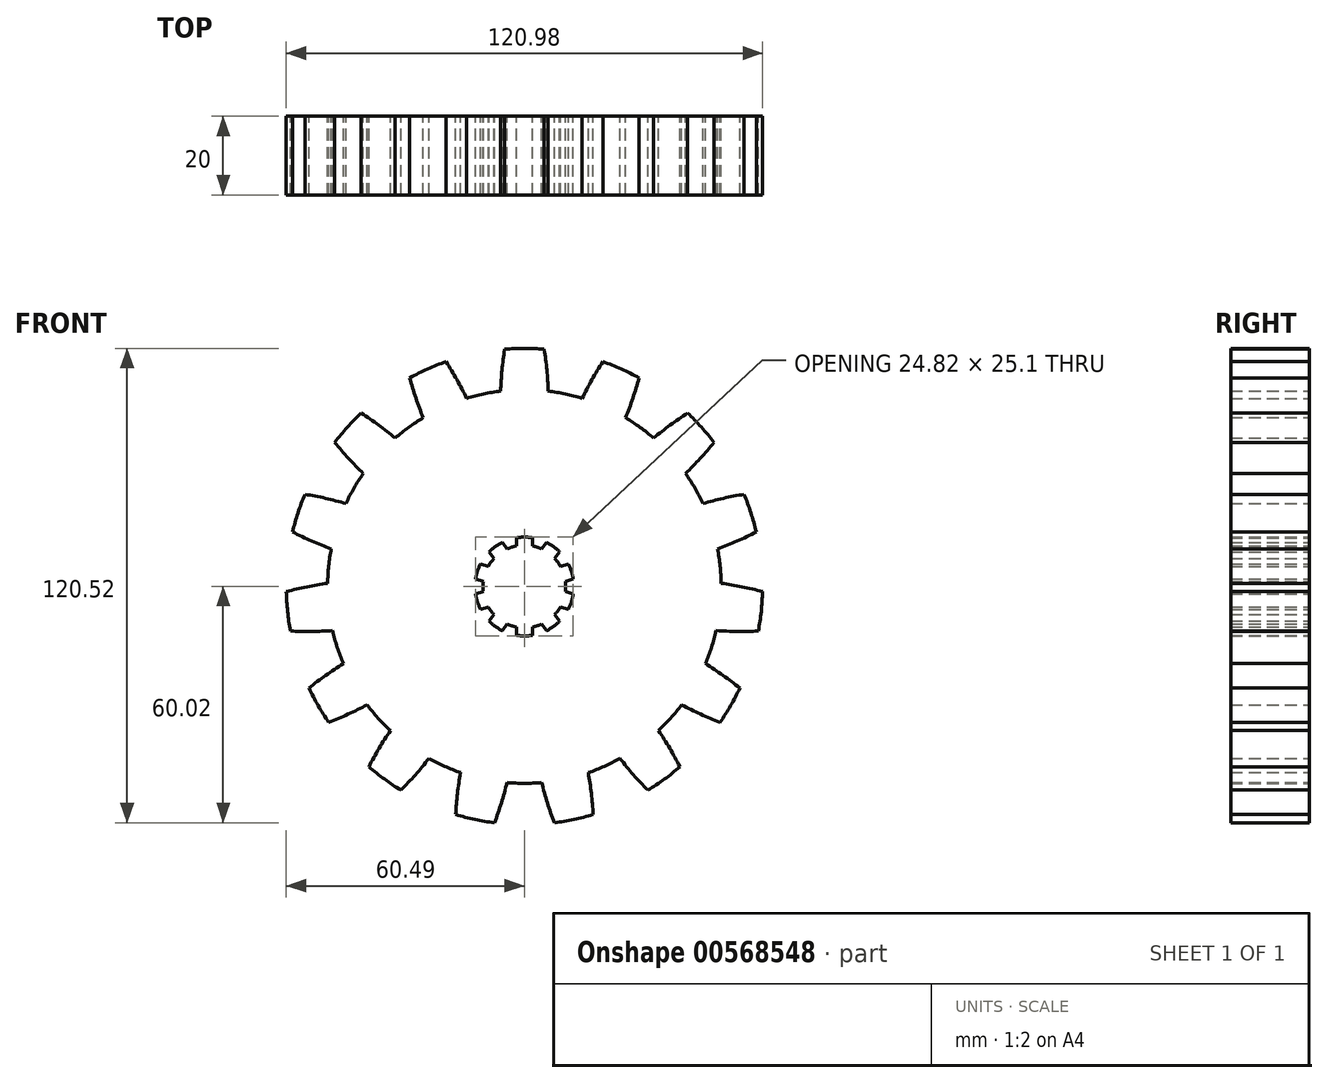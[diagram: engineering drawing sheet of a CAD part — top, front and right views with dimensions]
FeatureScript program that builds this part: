
annotation { "Feature Type Name" : "Feature", "Feature Type Description" : "" }
export const myFeature = defineFeature(function(context is Context, id is Id, definition is map)
    precondition{}
    {
        {
            var Q0;
            Q0=qCreatedBy(makeId("Front.planeOp"),FACE);
            var sketch = newSketch(context, id + "F0", { "sketchPlane" : qUnion([Q0])});
            skArc(sketch, "E0", {"start": v(-49.07, 9.59) * mm, "mid": v(-49.73, 5.23) * mm, "end": v(-50, 0.82) * mm});
            skLineSegment(sketch, "E1", {"start": v(0, 54.02) * mm, "end": v(0, -56.45) * mm, "construction": true});
            skLineSegment(sketch, "E2", {"start": v(-55.52, 46.5) * mm, "end": v(83.9, 46.5) * mm, "construction": true});
            skArc(sketch, "E3", {"start": v(5.04, 60.29) * mm, "mid": v(0, 60.5) * mm, "end": v(-5.04, 60.29) * mm});
            skArc(sketch, "E4.trimOffspring", {"start": v(-5.04, 60.29) * mm, "mid": v(-5.7, 54.98) * mm, "end": v(-6.05, 49.63) * mm});
            skArc(sketch, "E5.MirrorCS", {"start": v(5.04, 60.29) * mm, "mid": v(5.7, 54.98) * mm, "end": v(6.05, 49.63) * mm});
            skArc(sketch, "E6.1.0", {"start": v(-19.92, 57.13) * mm, "mid": v(-17.15, 52.54) * mm, "end": v(-14.66, 47.8) * mm});
            skArc(sketch, "E6.1.1", {"start": v(-29.12, 53.03) * mm, "mid": v(-27.57, 47.9) * mm, "end": v(-25.71, 42.88) * mm});
            skArc(sketch, "E6.1.2", {"start": v(-19.92, 57.13) * mm, "mid": v(-24.6, 55.27) * mm, "end": v(-29.12, 53.03) * mm});
            skArc(sketch, "E6.2.0", {"start": v(-41.43, 44.09) * mm, "mid": v(-37.04, 41.02) * mm, "end": v(-32.84, 37.7) * mm});
            skArc(sketch, "E6.2.1", {"start": v(-48.17, 36.6) * mm, "mid": v(-44.67, 32.55) * mm, "end": v(-40.93, 28.72) * mm});
            skArc(sketch, "E6.2.2", {"start": v(-41.43, 44.09) * mm, "mid": v(-44.96, 40.48) * mm, "end": v(-48.17, 36.6) * mm});
            skArc(sketch, "E6.3.0", {"start": v(-55.78, 23.42) * mm, "mid": v(-50.52, 22.4) * mm, "end": v(-45.34, 21.09) * mm});
            skArc(sketch, "E6.3.1", {"start": v(-58.9, 13.84) * mm, "mid": v(-54.05, 11.57) * mm, "end": v(-49.07, 9.59) * mm});
            skArc(sketch, "E6.3.2", {"start": v(-55.78, 23.42) * mm, "mid": v(-57.54, 18.7) * mm, "end": v(-58.9, 13.84) * mm});
            skArc(sketch, "E6.4.0", {"start": v(-60.49, -1.3) * mm, "mid": v(-55.27, -0.08) * mm, "end": v(-50, 0.82) * mm});
            skArc(sketch, "E6.4.1", {"start": v(-59.43, -11.31) * mm, "mid": v(-54.08, -11.42) * mm, "end": v(-48.73, -11.2) * mm});
            skArc(sketch, "E6.4.2", {"start": v(-60.49, -1.3) * mm, "mid": v(-60.17, -6.32) * mm, "end": v(-59.43, -11.31) * mm});
            skArc(sketch, "E6.5.0", {"start": v(-54.73, -25.78) * mm, "mid": v(-50.46, -22.55) * mm, "end": v(-46, -19.58) * mm});
            skArc(sketch, "E6.5.1", {"start": v(-49.7, -34.5) * mm, "mid": v(-44.76, -32.42) * mm, "end": v(-39.96, -30.05) * mm});
            skArc(sketch, "E6.5.2", {"start": v(-54.73, -25.78) * mm, "mid": v(-52.4, -30.25) * mm, "end": v(-49.7, -34.5) * mm});
            skArc(sketch, "E6.6.0", {"start": v(-39.51, -45.81) * mm, "mid": v(-36.93, -41.13) * mm, "end": v(-34.06, -36.6) * mm});
            skArc(sketch, "E6.6.1", {"start": v(-31.36, -51.74) * mm, "mid": v(-27.7, -47.83) * mm, "end": v(-24.28, -43.7) * mm});
            skArc(sketch, "E6.6.2", {"start": v(-39.51, -45.81) * mm, "mid": v(-35.56, -48.95) * mm, "end": v(-31.36, -51.74) * mm});
            skArc(sketch, "E6.7.0", {"start": v(-17.46, -57.93) * mm, "mid": v(-17, -52.6) * mm, "end": v(-16.23, -47.3) * mm});
            skArc(sketch, "E6.7.1", {"start": v(-7.6, -60.02) * mm, "mid": v(-5.85, -54.96) * mm, "end": v(-4.4, -49.8) * mm});
            skArc(sketch, "E6.7.2", {"start": v(-17.46, -57.93) * mm, "mid": v(-12.58, -59.18) * mm, "end": v(-7.6, -60.02) * mm});
            skArc(sketch, "E6.8.0", {"start": v(7.6, -60.02) * mm, "mid": v(5.85, -54.96) * mm, "end": v(4.4, -49.8) * mm});
            skArc(sketch, "E6.8.1", {"start": v(17.46, -57.93) * mm, "mid": v(17, -52.6) * mm, "end": v(16.23, -47.3) * mm});
            skArc(sketch, "E6.8.2", {"start": v(7.6, -60.02) * mm, "mid": v(12.58, -59.18) * mm, "end": v(17.46, -57.93) * mm});
            skArc(sketch, "E6.9.0", {"start": v(31.36, -51.74) * mm, "mid": v(27.7, -47.83) * mm, "end": v(24.28, -43.7) * mm});
            skArc(sketch, "E6.9.1", {"start": v(39.51, -45.81) * mm, "mid": v(36.93, -41.13) * mm, "end": v(34.06, -36.6) * mm});
            skArc(sketch, "E6.9.2", {"start": v(31.36, -51.74) * mm, "mid": v(35.56, -48.95) * mm, "end": v(39.51, -45.81) * mm});
            skArc(sketch, "E6.10.0", {"start": v(49.7, -34.5) * mm, "mid": v(44.76, -32.42) * mm, "end": v(39.96, -30.05) * mm});
            skArc(sketch, "E6.10.1", {"start": v(54.73, -25.78) * mm, "mid": v(50.46, -22.55) * mm, "end": v(46, -19.58) * mm});
            skArc(sketch, "E6.10.2", {"start": v(49.7, -34.5) * mm, "mid": v(52.4, -30.25) * mm, "end": v(54.73, -25.78) * mm});
            skArc(sketch, "E6.11.0", {"start": v(59.43, -11.31) * mm, "mid": v(54.08, -11.42) * mm, "end": v(48.73, -11.2) * mm});
            skArc(sketch, "E6.11.1", {"start": v(60.49, -1.3) * mm, "mid": v(55.27, -0.08) * mm, "end": v(50, 0.82) * mm});
            skArc(sketch, "E6.11.2", {"start": v(59.43, -11.31) * mm, "mid": v(60.17, -6.32) * mm, "end": v(60.49, -1.3) * mm});
            skArc(sketch, "E6.12.0", {"start": v(58.9, 13.84) * mm, "mid": v(54.05, 11.57) * mm, "end": v(49.07, 9.59) * mm});
            skArc(sketch, "E6.12.1", {"start": v(55.78, 23.42) * mm, "mid": v(50.52, 22.4) * mm, "end": v(45.34, 21.09) * mm});
            skArc(sketch, "E6.12.2", {"start": v(58.9, 13.84) * mm, "mid": v(57.54, 18.7) * mm, "end": v(55.78, 23.42) * mm});
            skArc(sketch, "E6.13.0", {"start": v(48.17, 36.6) * mm, "mid": v(44.67, 32.55) * mm, "end": v(40.93, 28.72) * mm});
            skArc(sketch, "E6.13.1", {"start": v(41.43, 44.09) * mm, "mid": v(37.04, 41.02) * mm, "end": v(32.84, 37.7) * mm});
            skArc(sketch, "E6.13.2", {"start": v(48.17, 36.6) * mm, "mid": v(44.96, 40.48) * mm, "end": v(41.43, 44.09) * mm});
            skArc(sketch, "E6.14.0", {"start": v(29.12, 53.03) * mm, "mid": v(27.57, 47.9) * mm, "end": v(25.71, 42.88) * mm});
            skArc(sketch, "E6.14.1", {"start": v(19.92, 57.13) * mm, "mid": v(17.15, 52.54) * mm, "end": v(14.66, 47.8) * mm});
            skArc(sketch, "E6.14.2", {"start": v(29.12, 53.03) * mm, "mid": v(24.6, 55.27) * mm, "end": v(19.92, 57.13) * mm});
            skArc(sketch, "E7.trimOffspring", {"start": v(-40.93, 28.72) * mm, "mid": v(-43.3, 25) * mm, "end": v(-45.34, 21.09) * mm});
            skArc(sketch, "E8.trimOffspring", {"start": v(-25.71, 42.88) * mm, "mid": v(-29.39, 40.45) * mm, "end": v(-32.84, 37.7) * mm});
            skArc(sketch, "E9.trimOffspring", {"start": v(-6.05, 49.63) * mm, "mid": v(-10.4, 48.9) * mm, "end": v(-14.66, 47.8) * mm});
            skArc(sketch, "E10.trimOffspring", {"start": v(14.66, 47.8) * mm, "mid": v(10.4, 48.9) * mm, "end": v(6.05, 49.63) * mm});
            skArc(sketch, "E11.trimOffspring", {"start": v(32.84, 37.7) * mm, "mid": v(29.39, 40.45) * mm, "end": v(25.71, 42.88) * mm});
            skArc(sketch, "E12.trimOffspring", {"start": v(45.34, 21.09) * mm, "mid": v(43.3, 25) * mm, "end": v(40.93, 28.72) * mm});
            skArc(sketch, "E13.trimOffspring", {"start": v(50, 0.82) * mm, "mid": v(49.73, 5.23) * mm, "end": v(49.07, 9.59) * mm});
            skArc(sketch, "E14.trimOffspring", {"start": v(46, -19.58) * mm, "mid": v(47.55, -15.45) * mm, "end": v(48.73, -11.2) * mm});
            skArc(sketch, "E15.trimOffspring", {"start": v(34.06, -36.6) * mm, "mid": v(37.16, -33.46) * mm, "end": v(39.96, -30.05) * mm});
            skArc(sketch, "E16.trimOffspring", {"start": v(16.23, -47.3) * mm, "mid": v(20.34, -45.68) * mm, "end": v(24.28, -43.7) * mm});
            skArc(sketch, "E17.trimOffspring", {"start": v(-4.4, -49.8) * mm, "mid": v(0, -50) * mm, "end": v(4.4, -49.8) * mm});
            skArc(sketch, "E18.trimOffspring", {"start": v(-24.28, -43.7) * mm, "mid": v(-20.34, -45.68) * mm, "end": v(-16.23, -47.3) * mm});
            skArc(sketch, "E19.trimOffspring", {"start": v(-39.96, -30.05) * mm, "mid": v(-37.16, -33.46) * mm, "end": v(-34.06, -36.6) * mm});
            skArc(sketch, "E20.trimOffspring", {"start": v(-48.73, -11.2) * mm, "mid": v(-47.55, -15.45) * mm, "end": v(-46, -19.58) * mm});
            skSolve(sketch);
        }
        {
            var Q0;
            Q0 = qSketchRegion(id + "F0", true);
            extrude(context, id + "F1", {"entities" : qUnion([Q0]), "depth" : 20 * mm, "offsetDistance" : 25 * mm});
        }
        {
            var Q0;
            Q0=qCreatedBy(makeId("Front.planeOp"),FACE);
            var sketch = newSketch(context, id + "F2", { "sketchPlane" : qUnion([Q0])});
            skCircle(sketch, "E21", {"center": v(0, 0) * mm, "radius": 10.5 * mm});
            skArc(sketch, "E22", {"start": v(2.05, 12.38) * mm, "mid": v(0, 12.55) * mm, "end": v(-2.05, 12.38) * mm});
            skLineSegment(sketch, "E23", {"start": v(2.05, 10.3) * mm, "end": v(2.05, 12.38) * mm});
            skLineSegment(sketch, "E24", {"start": v(-2.05, 10.3) * mm, "end": v(-2.05, 12.38) * mm});
            skArc(sketch, "E25.1.0", {"start": v(-5.62, 11.22) * mm, "mid": v(-7.38, 10.15) * mm, "end": v(-8.94, 8.81) * mm});
            skLineSegment(sketch, "E25.1.1", {"start": v(-4.4, 9.54) * mm, "end": v(-5.62, 11.22) * mm});
            skLineSegment(sketch, "E25.1.2", {"start": v(-7.71, 7.13) * mm, "end": v(-8.94, 8.81) * mm});
            skArc(sketch, "E25.2.0", {"start": v(-11.14, 5.78) * mm, "mid": v(-11.94, 3.88) * mm, "end": v(-12.4, 1.88) * mm});
            skLineSegment(sketch, "E25.2.1", {"start": v(-9.16, 5.13) * mm, "end": v(-11.14, 5.78) * mm});
            skLineSegment(sketch, "E25.2.2", {"start": v(-10.43, 1.23) * mm, "end": v(-12.4, 1.88) * mm});
            skArc(sketch, "E25.3.0", {"start": v(-12.4, -1.88) * mm, "mid": v(-11.94, -3.88) * mm, "end": v(-11.14, -5.78) * mm});
            skLineSegment(sketch, "E25.3.1", {"start": v(-10.43, -1.23) * mm, "end": v(-12.4, -1.88) * mm});
            skLineSegment(sketch, "E25.3.2", {"start": v(-9.16, -5.13) * mm, "end": v(-11.14, -5.78) * mm});
            skArc(sketch, "E25.4.0", {"start": v(-8.94, -8.81) * mm, "mid": v(-7.38, -10.15) * mm, "end": v(-5.62, -11.22) * mm});
            skLineSegment(sketch, "E25.4.1", {"start": v(-7.71, -7.13) * mm, "end": v(-8.94, -8.81) * mm});
            skLineSegment(sketch, "E25.4.2", {"start": v(-4.4, -9.54) * mm, "end": v(-5.62, -11.22) * mm});
            skArc(sketch, "E25.5.0", {"start": v(-2.05, -12.38) * mm, "mid": v(0, -12.55) * mm, "end": v(2.05, -12.38) * mm});
            skLineSegment(sketch, "E25.5.1", {"start": v(-2.05, -10.3) * mm, "end": v(-2.05, -12.38) * mm});
            skLineSegment(sketch, "E25.5.2", {"start": v(2.05, -10.3) * mm, "end": v(2.05, -12.38) * mm});
            skArc(sketch, "E25.6.0", {"start": v(5.62, -11.22) * mm, "mid": v(7.38, -10.15) * mm, "end": v(8.94, -8.81) * mm});
            skLineSegment(sketch, "E25.6.1", {"start": v(4.4, -9.54) * mm, "end": v(5.62, -11.22) * mm});
            skLineSegment(sketch, "E25.6.2", {"start": v(7.71, -7.13) * mm, "end": v(8.94, -8.81) * mm});
            skArc(sketch, "E25.7.0", {"start": v(11.14, -5.78) * mm, "mid": v(11.94, -3.88) * mm, "end": v(12.4, -1.88) * mm});
            skLineSegment(sketch, "E25.7.1", {"start": v(9.16, -5.13) * mm, "end": v(11.14, -5.78) * mm});
            skLineSegment(sketch, "E25.7.2", {"start": v(10.43, -1.23) * mm, "end": v(12.4, -1.88) * mm});
            skArc(sketch, "E25.8.0", {"start": v(12.4, 1.88) * mm, "mid": v(11.94, 3.88) * mm, "end": v(11.14, 5.78) * mm});
            skLineSegment(sketch, "E25.8.1", {"start": v(10.43, 1.23) * mm, "end": v(12.4, 1.88) * mm});
            skLineSegment(sketch, "E25.8.2", {"start": v(9.16, 5.13) * mm, "end": v(11.14, 5.78) * mm});
            skArc(sketch, "E25.9.0", {"start": v(8.94, 8.81) * mm, "mid": v(7.38, 10.15) * mm, "end": v(5.62, 11.22) * mm});
            skLineSegment(sketch, "E25.9.1", {"start": v(7.71, 7.13) * mm, "end": v(8.94, 8.81) * mm});
            skLineSegment(sketch, "E25.9.2", {"start": v(4.4, 9.54) * mm, "end": v(5.62, 11.22) * mm});
            skSolve(sketch);
        }
        {
            var Q0;
            Q0 = qSketchRegion(id + "F2", true);
            extrude(context, id + "F3", {"entities" : qUnion([Q0]), "operationType" : NewBodyOperationType.REMOVE, "depth" : 20 * mm, "offsetDistance" : 25 * mm});
        }
    });
